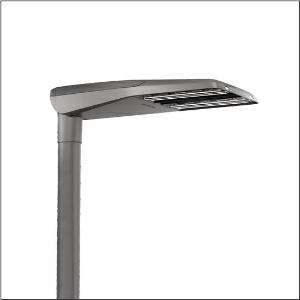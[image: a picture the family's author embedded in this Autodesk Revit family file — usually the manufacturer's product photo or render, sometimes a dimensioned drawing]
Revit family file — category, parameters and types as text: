
# Revit family: streetlight_sl_11_iq_midi___st1_2p1_0_5xc3g51f08me_c537
name_source: partatom
category: Lighting Fixtures
units: mm (PartAtom-declared; Revit-internal decimal feet)

## family parameters
Cut with Voids When Loaded = No
Host = Face
Light Source = No
Part Type = Normal
Room Calculation Point = No
Round Connector Dimension = Use Diameter
Shared = No

## types (1)
- --- (1 x LED, 17750 lm, 124.7 W, 3000K)
    Apparent Load = 125 VA
    CIE Flux Codes = 31 68 95 100 100
    Color Rendering = 70
    Color Temperature = 3000K
    Default Elevation = 1800 mm
    Description = Streetlight SL 11 iQ midi, mast luminaire, primary light control with 3 zone facetted reflector, of plastic, silver coated, highly specular, primary optical cover: cover, of PMMA, transparent, light distribution: ST1.2P1.0, light emission: direct distribution, primary light characteristic: asymmetric, installation type: post-top, side-entry, LED, High Power LED, rated luminous flux: 17.750lm, luminous efficacy: 142lm/W, light colour: 730, colour temperature: 3000K, control: Street-Remote, optimised constant luminous flux control (CLO 2.0), Auto-Match, Desk-Remote (wireless, voltage-free reading and setting of iQ features in the workshop via application-optimized NFC function/RFID function), Light-Fading, Smart-Wire, Night-Set, Lumen-Switch, Temp-Guard, with cable H07RN-F 5x 1.5mm², mains connection: 230..240V, AC, 50/60Hz, connection cable pre-assembled, cable length: 12,5m, start of lifetime: 125W, end of service life: 132W, reduction: 57W, luminaire housing, of diecast aluminium, powder-coated, Siteco® metallic grey (DB 702S), please order mast flange separately, inclination adjustable without tools: 0°, 5°, 10°, 15° (post-top) | 0°, -5°, -10°, -15° (side-entry), sealing non-destructively replaceable, multi-level sealing system, length: 780mm, width: 376mm, height: 118mm, mast flange for spigot size: 42mm (side-entry): 5XC10008XM4, 60/48mm (side-entry/post-top): 5XC10108XM2, 76/60mm (side-entry/post-top): 5XC10108XM1, equipment: Power, protection rating (complete): IP66, insulation class (complete): insulation class II (safety insulation), certification: CE, ENEC, VDE, impact resistance: IK09, permissible operating ambient temperature for outdoor applications: -25..+50°C, standard-compliant lighting for roads and squares, Environmental Product Declaration (EPD) tested and certified by an independent institute, packaging unit: 1 piece

Light Distribution: ST1.2P1.0
    Height = 118 mm
    Lamp = 1 x LED
    Lamp Light Flux = 17750 lm
    Lamp Power = 124.7 W
    Lamp count = 1
    Length = 780 mm
    Luminous efficacy = 142 lm/W
    Manufacturer = Siteco
    ModVariant = No
    Model = 5XC3G51F08ME
    Number of Poles = 1
    OnlyDefault = Yes
    Power Factor = 1
    Product Name = Streetlight SL 11 iQ midi | ST1.2P1.0
    Product group = mast luminaire | pylon top
    ProductGroupID = 6100
    Protection Class = Protection class II
    Protection Degree = IP 66
    RLX_Detail_Level = 1
    RLX_Emergency_Light_Flux = 0 lm
    RLX_Emergency_Type = 0
    RLX_Emergency_Type_DB = No
    RlxData = <blob elided: 70681 chars, md5=10c1870c>
    Socket = socket
    Standby Power = 0 W
    System Light Flux = 17750 lm
    System Power = 125 W
    Type Comments = factory setting: luminous flux: 100 % | dim-lin: 254 | 557 mA
    Type Image = l_1005960.jpg
    URL = http://relux.com
    VarID = @adj_147503
    Voltage = 0 V
    Weight = 0.00 kg
    Width = 376 mm

## geometry (parser evidence)
native form markers: Blend x4, Sweep x9
no freeform markers — native parametric forms only
